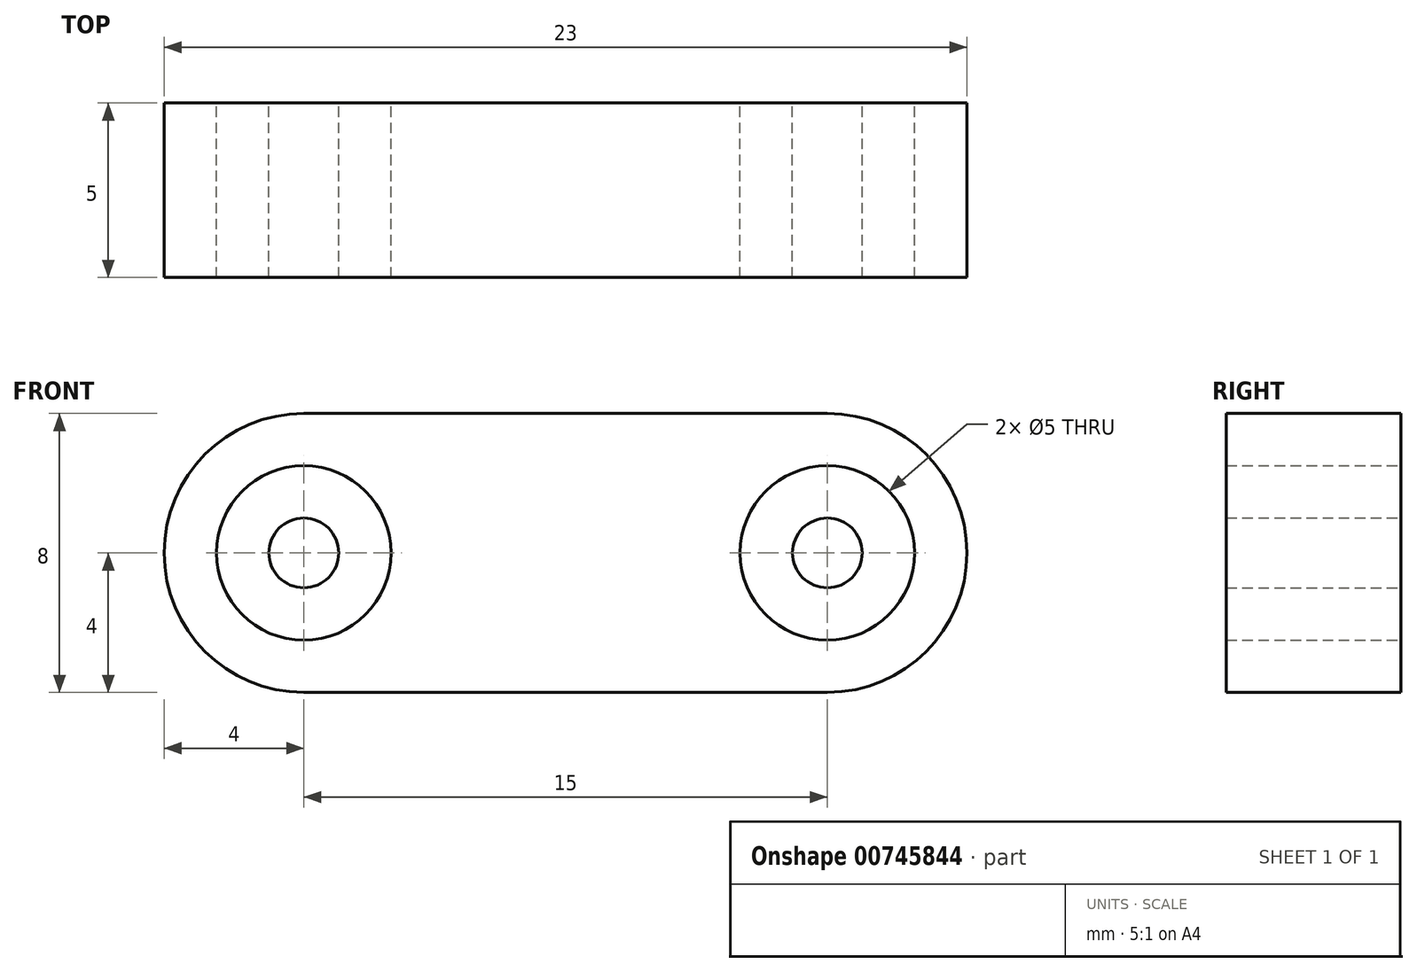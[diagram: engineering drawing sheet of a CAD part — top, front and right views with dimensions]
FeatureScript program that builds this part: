
annotation { "Feature Type Name" : "Feature", "Feature Type Description" : "" }
export const myFeature = defineFeature(function(context is Context, id is Id, definition is map)
    precondition{}
    {
        {
            var Q0;
            Q0=qCreatedBy(makeId("Front.planeOp"),FACE);
            var sketch = newSketch(context, id + "F0", { "sketchPlane" : qUnion([Q0])});
            skCircle(sketch, "E0", {"center": v(0, 0) * mm, "radius": 1 * mm});
            skCircle(sketch, "E1", {"center": v(0, 0) * mm, "radius": 2.5 * mm});
            skArc(sketch, "E2", {"start": v(0, 4) * mm, "mid": v(-4, 0) * mm, "end": v(0, -4) * mm});
            skCircle(sketch, "E3", {"center": v(15, 0) * mm, "radius": 1 * mm});
            skCircle(sketch, "E4", {"center": v(15, 0) * mm, "radius": 2.5 * mm});
            skArc(sketch, "E5", {"start": v(15, -4) * mm, "mid": v(19, 0) * mm, "end": v(15, 4) * mm});
            skLineSegment(sketch, "E6", {"start": v(0, 4) * mm, "end": v(15, 4) * mm});
            skLineSegment(sketch, "E7", {"start": v(0, -4) * mm, "end": v(15, -4) * mm});
            skSolve(sketch);
        }
        {
            var Q0;
            Q0 = qSketchRegion(id + "F0", true);
            var Q1;
            Q1=makeQuery(id+"F0.imprint","IMPRINT",FACE,{"disambiguationData":[TD([[makeQuery(id+"F0.imprint","IMPRINT",EDGE,{"derivedFrom":sQuery(id+"F0.wireOp",EDGE,"E0")}),1.0]])]});
            var Q2;
            Q2=makeQuery(id+"F0.imprint","IMPRINT",FACE,{"disambiguationData":[TD([[makeQuery(id+"F0.imprint","IMPRINT",EDGE,{"derivedFrom":sQuery(id+"F0.wireOp",EDGE,"E3")}),1.0]])]});
            extrude(context, id + "F1", {"entities" : qUnion([Q0, Q1, Q2]), "depth" : 5 * mm, "offsetDistance" : 25.4 * mm});
        }
    });
